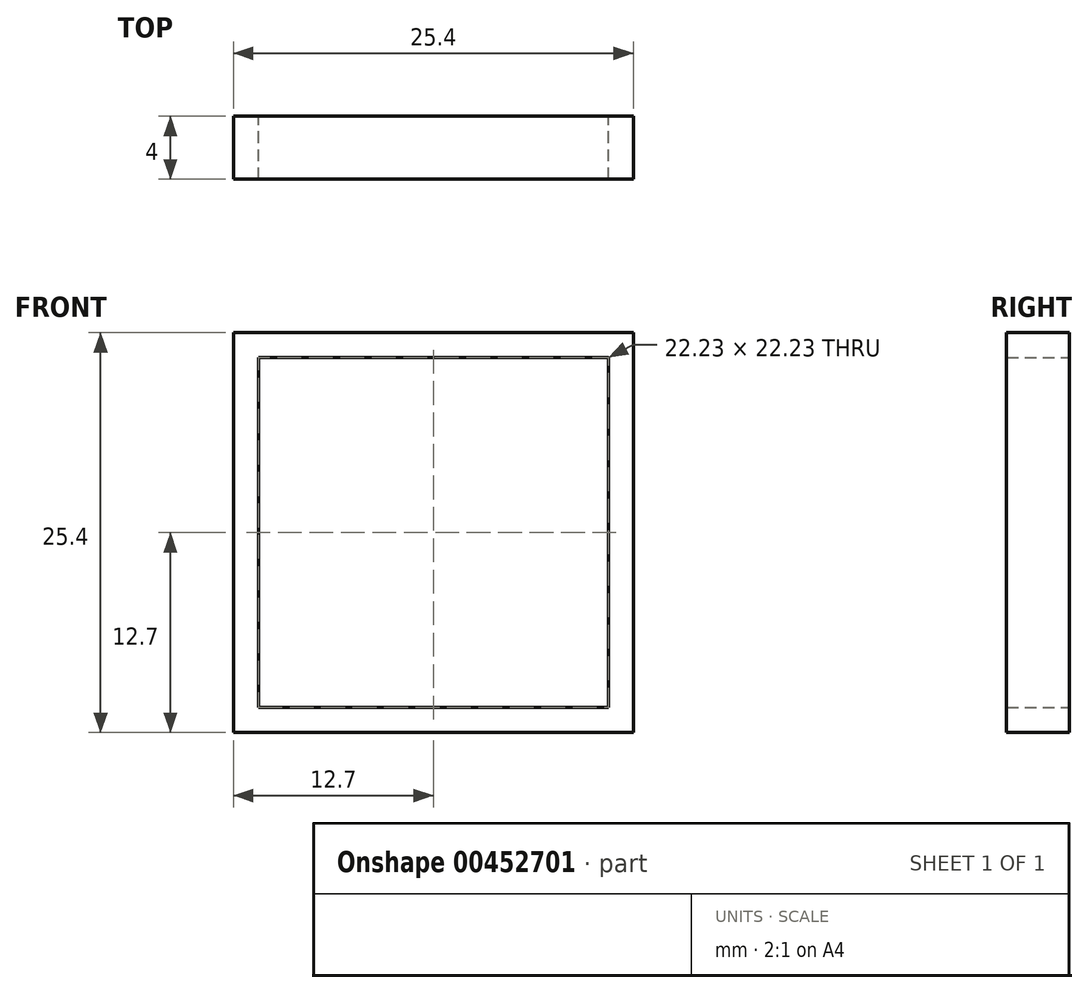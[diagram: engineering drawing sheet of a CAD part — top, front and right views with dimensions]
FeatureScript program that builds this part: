
annotation { "Feature Type Name" : "Feature", "Feature Type Description" : "" }
export const myFeature = defineFeature(function(context is Context, id is Id, definition is map)
    precondition{}
    {
        {
            assignVariable(context, id + "F0", {"name" : "XL", "anyValue" : 4});
        }
        {
            var Q0;
            Q0=qCreatedBy(makeId("Front.planeOp"),FACE);
            var sketch = newSketch(context, id + "F1", { "sketchPlane" : qUnion([Q0])});
            skLineSegment(sketch, "E0.bottom", {"start": v(-12.7, 12.7) * mm, "end": v(12.7, 12.7) * mm});
            skLineSegment(sketch, "E0.top", {"start": v(-12.7, -12.7) * mm, "end": v(12.7, -12.7) * mm});
            skLineSegment(sketch, "E0.left", {"start": v(-12.7, 12.7) * mm, "end": v(-12.7, -12.7) * mm});
            skLineSegment(sketch, "E0.right", {"start": v(12.7, 12.7) * mm, "end": v(12.7, -12.7) * mm});
            skPoint(sketch, "E0.middle", {"position": v(0, 0) * mm});
            skLineSegment(sketch, "E1.bottom", {"start": v(-11.11, -11.11) * mm, "end": v(11.11, -11.11) * mm});
            skLineSegment(sketch, "E1.top", {"start": v(-11.11, 11.11) * mm, "end": v(11.11, 11.11) * mm});
            skLineSegment(sketch, "E1.left", {"start": v(-11.11, -11.11) * mm, "end": v(-11.11, 11.11) * mm});
            skLineSegment(sketch, "E1.right", {"start": v(11.11, -11.11) * mm, "end": v(11.11, 11.11) * mm});
            skSolve(sketch);
        }
        {
            var Q0;
            Q0=makeQuery(id+"F1.imprint","IMPRINT",FACE,{"disambiguationData":[TD([[makeQuery(id+"F1.imprint","IMPRINT",EDGE,{"derivedFrom":sQuery(id+"F1.wireOp",EDGE,"E0.bottom")}),-1.0]])]});
            extrude(context, id + "F2", {"entities" : qUnion([Q0]), "depth" : (getVariable(context, 'XL')) * mm});
        }
    });
